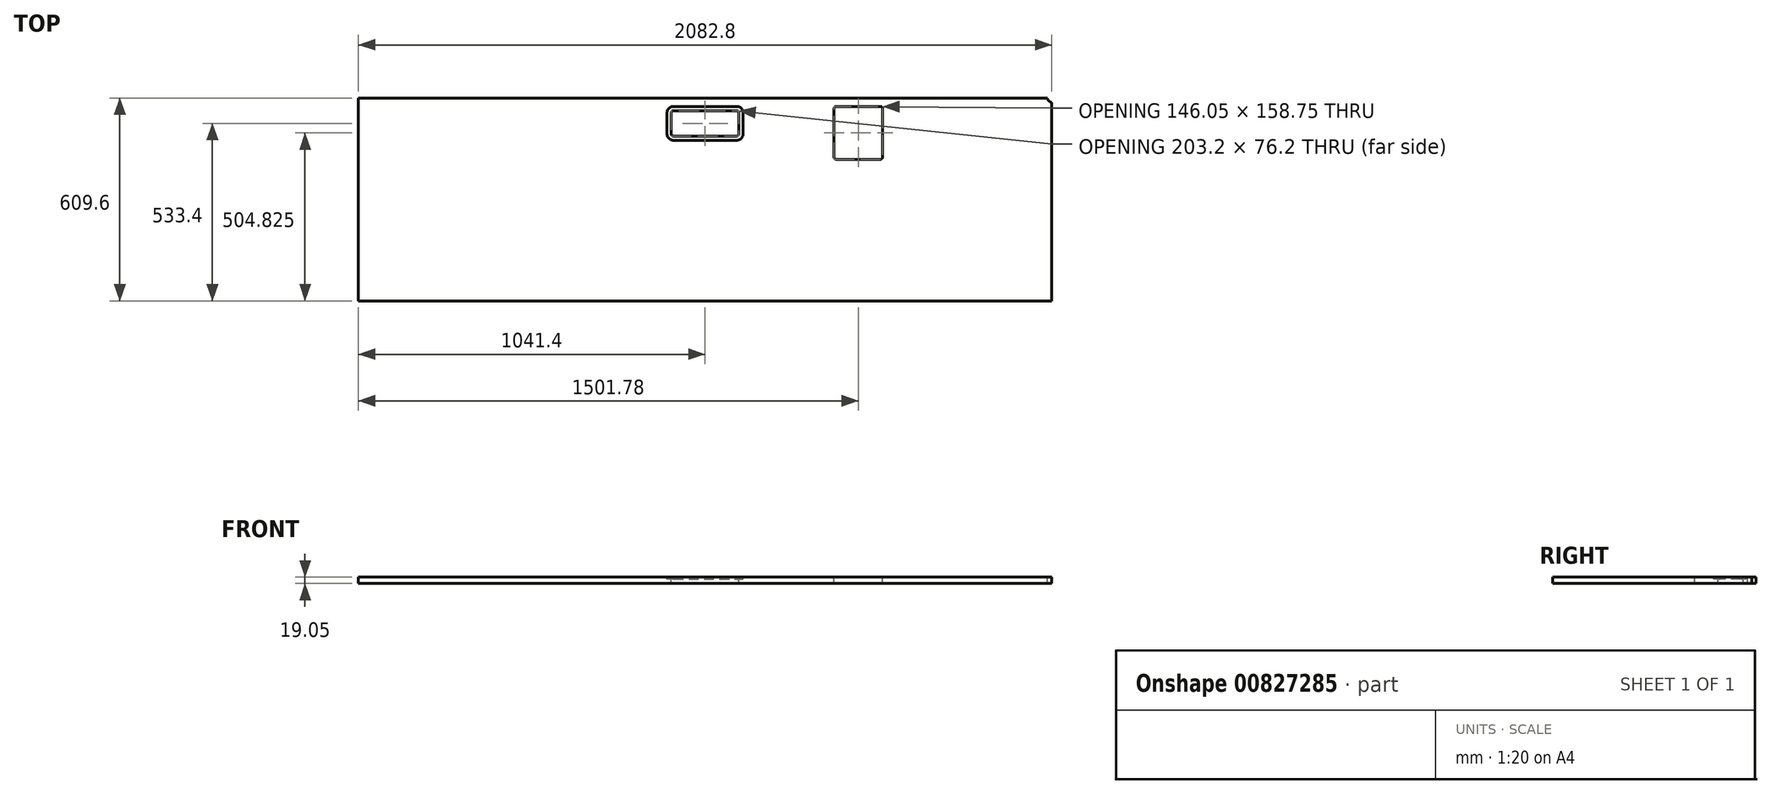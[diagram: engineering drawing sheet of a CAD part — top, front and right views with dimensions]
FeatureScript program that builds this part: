
annotation { "Feature Type Name" : "Feature", "Feature Type Description" : "" }
export const myFeature = defineFeature(function(context is Context, id is Id, definition is map)
    precondition{}
    {
        {
            var Q0;
            Q0=qCreatedBy(makeId("Top.planeOp"),FACE);
            var sketch = newSketch(context, id + "F0", { "sketchPlane" : qUnion([Q0])});
            skLineSegment(sketch, "E0.bottom", {"start": v(0, 0) * mm, "end": v(2082.8, 0) * mm});
            skLineSegment(sketch, "E0.top", {"start": v(0, 609.6) * mm, "end": v(2082.8, 609.6) * mm});
            skLineSegment(sketch, "E0.left", {"start": v(0, 0) * mm, "end": v(0, 609.6) * mm});
            skLineSegment(sketch, "E0.right", {"start": v(2082.8, 0) * mm, "end": v(2082.8, 609.6) * mm});
            skSolve(sketch);
        }
        {
            var Q0;
            Q0 = qSketchRegion(id + "F0", true);
            extrude(context, id + "F1", {"entities" : qUnion([Q0]), "depth" : 19.05 * mm, "offsetDistance" : 25.4 * mm});
        }
        {
            var Q0;
            Q0=makeQuery(id+"F1.opExtrude","CAP_FACE",FACE,{"disambiguationData":[OSD([sQuery(id+"F0.wireOp",EDGE,"E0.bottom"),sQuery(id+"F0.wireOp",EDGE,"E0.top"),sQuery(id+"F0.wireOp",EDGE,"E0.left"),sQuery(id+"F0.wireOp",EDGE,"E0.right")])],"isStart":false});
            var sketch = newSketch(context, id + "F2", { "sketchPlane" : qUnion([Q0])});
            skLineSegment(sketch, "E1.bottom", {"start": v(1435.1, 584.2) * mm, "end": v(1568.45, 584.2) * mm});
            skLineSegment(sketch, "E1.top", {"start": v(1435.1, 425.45) * mm, "end": v(1568.45, 425.45) * mm});
            skLineSegment(sketch, "E1.left", {"start": v(1428.75, 577.85) * mm, "end": v(1428.75, 431.8) * mm});
            skLineSegment(sketch, "E1.right", {"start": v(1574.8, 577.85) * mm, "end": v(1574.8, 431.8) * mm});
            skLineSegment(sketch, "E2.bottom", {"start": v(946.15, 571.5) * mm, "end": v(1136.65, 571.5) * mm});
            skLineSegment(sketch, "E2.top", {"start": v(946.15, 495.3) * mm, "end": v(1136.65, 495.3) * mm});
            skLineSegment(sketch, "E2.left", {"start": v(939.8, 565.15) * mm, "end": v(939.8, 501.65) * mm});
            skLineSegment(sketch, "E2.right", {"start": v(1143, 565.15) * mm, "end": v(1143, 501.65) * mm});
            skLineSegment(sketch, "E3", {"start": v(41.27, 609.6) * mm, "end": v(41.28, 0) * mm, "construction": true});
            skLineSegment(sketch, "E4", {"start": v(60.32, 609.6) * mm, "end": v(60.33, 0) * mm, "construction": true});
            skLineSegment(sketch, "E5.1.0.0", {"start": v(720.73, 609.6) * mm, "end": v(720.73, 0) * mm, "construction": true});
            skLineSegment(sketch, "E5.1.0.1", {"start": v(701.68, 609.6) * mm, "end": v(701.68, 0) * mm, "construction": true});
            skLineSegment(sketch, "E5.2.0.0", {"start": v(1381.13, 609.6) * mm, "end": v(1381.13, 0) * mm, "construction": true});
            skLineSegment(sketch, "E5.2.0.1", {"start": v(1362.08, 609.6) * mm, "end": v(1362.08, 0) * mm, "construction": true});
            skLineSegment(sketch, "E5.3.0.0", {"start": v(2041.53, 609.6) * mm, "end": v(2041.53, 0) * mm, "construction": true});
            skLineSegment(sketch, "E5.3.0.1", {"start": v(2022.48, 609.6) * mm, "end": v(2022.48, 0) * mm, "construction": true});
            skLineSegment(sketch, "E5.direction1", {"start": v(41.28, 0) * mm, "end": v(701.68, 0) * mm, "construction": true});
            skPoint(sketch, "E6.visualSharp", {"position": v(1143, 571.5) * mm});
            skArc(sketch, "E6.filletArc", {"start": v(1143, 565.15) * mm, "mid": v(1141.14, 569.64) * mm, "end": v(1136.65, 571.5) * mm});
            skPoint(sketch, "E7.visualSharp", {"position": v(1143, 495.3) * mm});
            skArc(sketch, "E7.filletArc", {"start": v(1136.65, 495.3) * mm, "mid": v(1141.14, 497.16) * mm, "end": v(1143, 501.65) * mm});
            skPoint(sketch, "E8.visualSharp", {"position": v(939.8, 495.3) * mm});
            skArc(sketch, "E8.filletArc", {"start": v(939.8, 501.65) * mm, "mid": v(941.66, 497.16) * mm, "end": v(946.15, 495.3) * mm});
            skPoint(sketch, "E9.visualSharp", {"position": v(939.8, 571.5) * mm});
            skArc(sketch, "E9.filletArc", {"start": v(946.15, 571.5) * mm, "mid": v(941.66, 569.64) * mm, "end": v(939.8, 565.15) * mm});
            skPoint(sketch, "E10.visualSharp", {"position": v(1428.75, 584.2) * mm});
            skArc(sketch, "E10.filletArc", {"start": v(1435.1, 584.2) * mm, "mid": v(1430.6, 582.34) * mm, "end": v(1428.75, 577.85) * mm});
            skPoint(sketch, "E11.visualSharp", {"position": v(1428.75, 425.45) * mm});
            skArc(sketch, "E11.filletArc", {"start": v(1428.75, 431.8) * mm, "mid": v(1430.6, 427.3) * mm, "end": v(1435.1, 425.45) * mm});
            skPoint(sketch, "E12.visualSharp", {"position": v(1574.8, 425.45) * mm});
            skArc(sketch, "E12.filletArc", {"start": v(1568.45, 425.45) * mm, "mid": v(1572.94, 427.3) * mm, "end": v(1574.8, 431.8) * mm});
            skPoint(sketch, "E13.visualSharp", {"position": v(1574.8, 584.2) * mm});
            skArc(sketch, "E13.filletArc", {"start": v(1574.8, 577.85) * mm, "mid": v(1572.94, 582.34) * mm, "end": v(1568.45, 584.2) * mm});
            skCircle(sketch, "E14", {"center": v(2082.8, 609.6) * mm, "radius": 12.7 * mm});
            skSolve(sketch);
        }
        {
            var Q0;
            Q0 = qSketchRegion(id + "F2", true);
            extrude(context, id + "F3", {"entities" : qUnion([Q0]), "operationType" : NewBodyOperationType.REMOVE, "oppositeDirection" : true, "depth" : 25.4 * mm, "offsetDistance" : 25.4 * mm});
        }
        {
            var Q0;
            Q0=makeQuery(id+"F1.opExtrude","CAP_FACE",FACE,{"disambiguationData":[OSD([sQuery(id+"F0.wireOp",EDGE,"E0.bottom"),sQuery(id+"F0.wireOp",EDGE,"E0.top"),sQuery(id+"F0.wireOp",EDGE,"E0.left"),sQuery(id+"F0.wireOp",EDGE,"E0.right")])],"isStart":false});
            var sketch = newSketch(context, id + "F4", { "sketchPlane" : qUnion([Q0])});
            skLineSegment(sketch, "E15.0", {"start": v(1143, 565.15) * mm, "end": v(1143, 501.65) * mm});
            skArc(sketch, "E15.1", {"start": v(1136.65, 495.3) * mm, "mid": v(1141.14, 497.16) * mm, "end": v(1143, 501.65) * mm});
            skLineSegment(sketch, "E15.2", {"start": v(946.15, 495.3) * mm, "end": v(1136.65, 495.3) * mm});
            skArc(sketch, "E15.3", {"start": v(939.8, 501.65) * mm, "mid": v(941.66, 497.16) * mm, "end": v(946.15, 495.3) * mm});
            skLineSegment(sketch, "E15.4", {"start": v(939.8, 565.15) * mm, "end": v(939.8, 501.65) * mm});
            skArc(sketch, "E15.5", {"start": v(946.15, 571.5) * mm, "mid": v(941.66, 569.64) * mm, "end": v(939.8, 565.15) * mm});
            skLineSegment(sketch, "E15.6", {"start": v(946.15, 571.5) * mm, "end": v(1136.65, 571.5) * mm});
            skArc(sketch, "E15.7", {"start": v(1143, 565.15) * mm, "mid": v(1141.14, 569.64) * mm, "end": v(1136.65, 571.5) * mm});
            skArc(sketch, "E16.0", {"start": v(946.15, 584.2) * mm, "mid": v(932.68, 578.62) * mm, "end": v(927.1, 565.15) * mm});
            skLineSegment(sketch, "E16.1", {"start": v(946.15, 584.2) * mm, "end": v(1136.65, 584.2) * mm});
            skLineSegment(sketch, "E16.2", {"start": v(927.1, 565.15) * mm, "end": v(927.1, 501.65) * mm});
            skArc(sketch, "E16.3", {"start": v(1155.7, 565.15) * mm, "mid": v(1150.12, 578.62) * mm, "end": v(1136.65, 584.2) * mm});
            skArc(sketch, "E16.4", {"start": v(927.1, 501.65) * mm, "mid": v(932.68, 488.18) * mm, "end": v(946.15, 482.6) * mm});
            skLineSegment(sketch, "E16.5", {"start": v(946.15, 482.6) * mm, "end": v(1136.65, 482.6) * mm});
            skArc(sketch, "E16.6", {"start": v(1136.65, 482.6) * mm, "mid": v(1150.12, 488.18) * mm, "end": v(1155.7, 501.65) * mm});
            skLineSegment(sketch, "E16.7", {"start": v(1155.7, 565.15) * mm, "end": v(1155.7, 501.65) * mm});
            skSolve(sketch);
        }
        {
            var Q0;
            Q0 = qSketchRegion(id + "F4", true);
            extrude(context, id + "F5", {"entities" : qUnion([Q0]), "operationType" : NewBodyOperationType.REMOVE, "oppositeDirection" : true, "depth" : 6.35 * mm, "offsetDistance" : 25.4 * mm});
        }
    });
